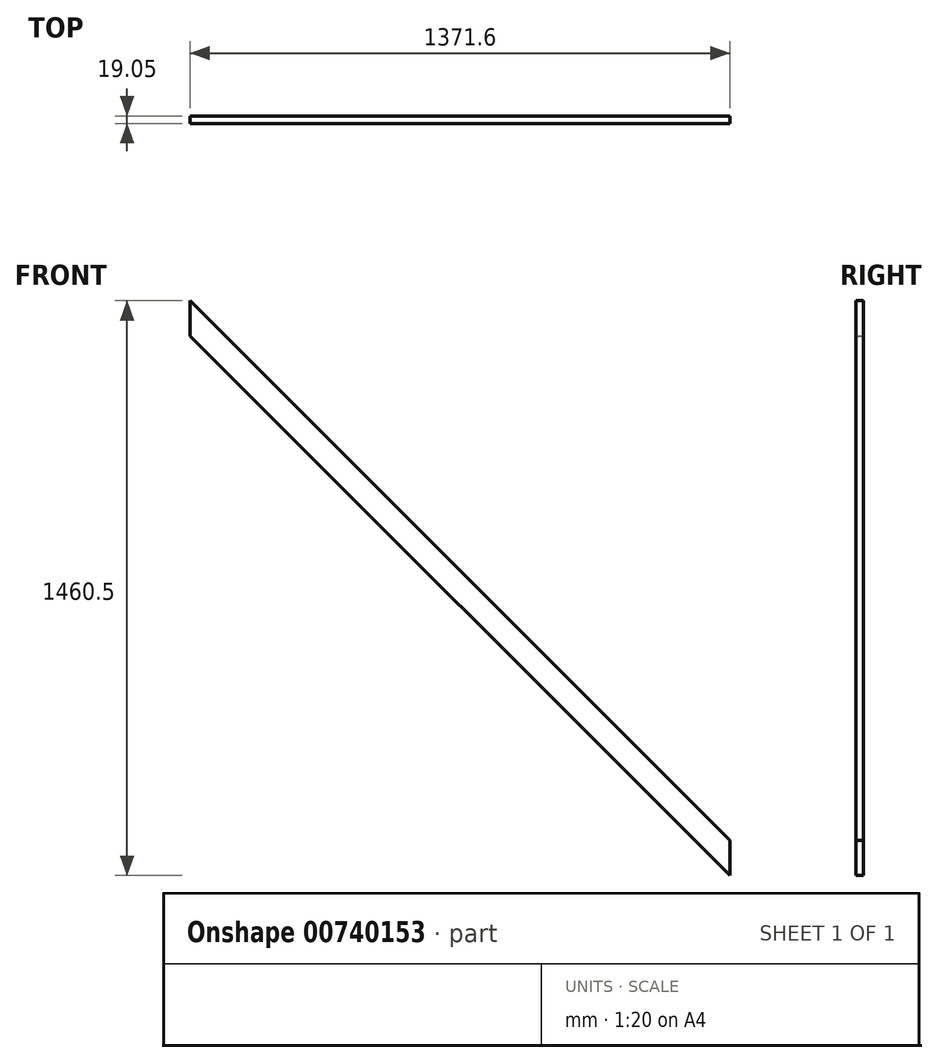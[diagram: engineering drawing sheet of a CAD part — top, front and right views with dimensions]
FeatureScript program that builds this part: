
annotation { "Feature Type Name" : "Feature", "Feature Type Description" : "" }
export const myFeature = defineFeature(function(context is Context, id is Id, definition is map)
    precondition{}
    {
        {
            var Q0;
            Q0=qCreatedBy(makeId("Front.planeOp"),FACE);
            var sketch = newSketch(context, id + "F0", { "sketchPlane" : qUnion([Q0])});
            skLineSegment(sketch, "E0.bottom", {"start": v(-488.78, 687.7) * mm, "end": v(882.82, 687.7) * mm});
            skLineSegment(sketch, "E0.top", {"start": v(-488.78, -772.8) * mm, "end": v(882.82, -772.8) * mm});
            skLineSegment(sketch, "E0.left", {"start": v(-488.78, 687.7) * mm, "end": v(-488.78, -772.8) * mm});
            skLineSegment(sketch, "E0.right", {"start": v(882.82, 687.7) * mm, "end": v(882.82, -772.8) * mm});
            skLineSegment(sketch, "E1.bottom", {"start": v(-488.78, 687.7) * mm, "end": v(927.7, -727.89) * mm});
            skLineSegment(sketch, "E1.top", {"start": v(-533.67, 642.78) * mm, "end": v(882.82, -772.8) * mm});
            skLineSegment(sketch, "E1.left", {"start": v(-488.78, 687.7) * mm, "end": v(-533.67, 642.78) * mm});
            skLineSegment(sketch, "E1.right", {"start": v(927.7, -727.89) * mm, "end": v(882.82, -772.8) * mm});
            skPoint(sketch, "E1.middle", {"position": v(197.02, -42.55) * mm});
            skPoint(sketch, "E1.middle.positionSnap0", {"position": v(197.02, 687.7) * mm});
            skPoint(sketch, "E1.middle.positionSnap1", {"position": v(-488.78, -42.55) * mm});
            skPoint(sketch, "E1.centerSnap0", {"position": v(197.02, 687.7) * mm});
            skPoint(sketch, "E1.centerSnap1", {"position": v(-488.78, -42.55) * mm});
            skSolve(sketch);
        }
        {
            var Q0;
            {var subQ1=sQuery(id+"F0.wireOp",EDGE,"E0.left");var subQ3=sQuery(id+"F0.wireOp",EDGE,"E1.top");var subQ4=makeQuery(id+"F0.imprint","INTERSECT",VERTEX,{"derivedFrom":[subQ1,subQ3]});Q0=makeQuery(id+"F0.imprint","IMPRINT",FACE,{"disambiguationData":[TD([[makeQuery(id+"F0.imprint","IMPRINT",EDGE,{"disambiguationData":[TD([[subQ4,1.0]])],"derivedFrom":subQ1}),1.0]])]});}
            extrude(context, id + "F1", {"entities" : qUnion([Q0]), "depth" : 19.05 * mm, "offsetDistance" : 25.4 * mm});
        }
    });
